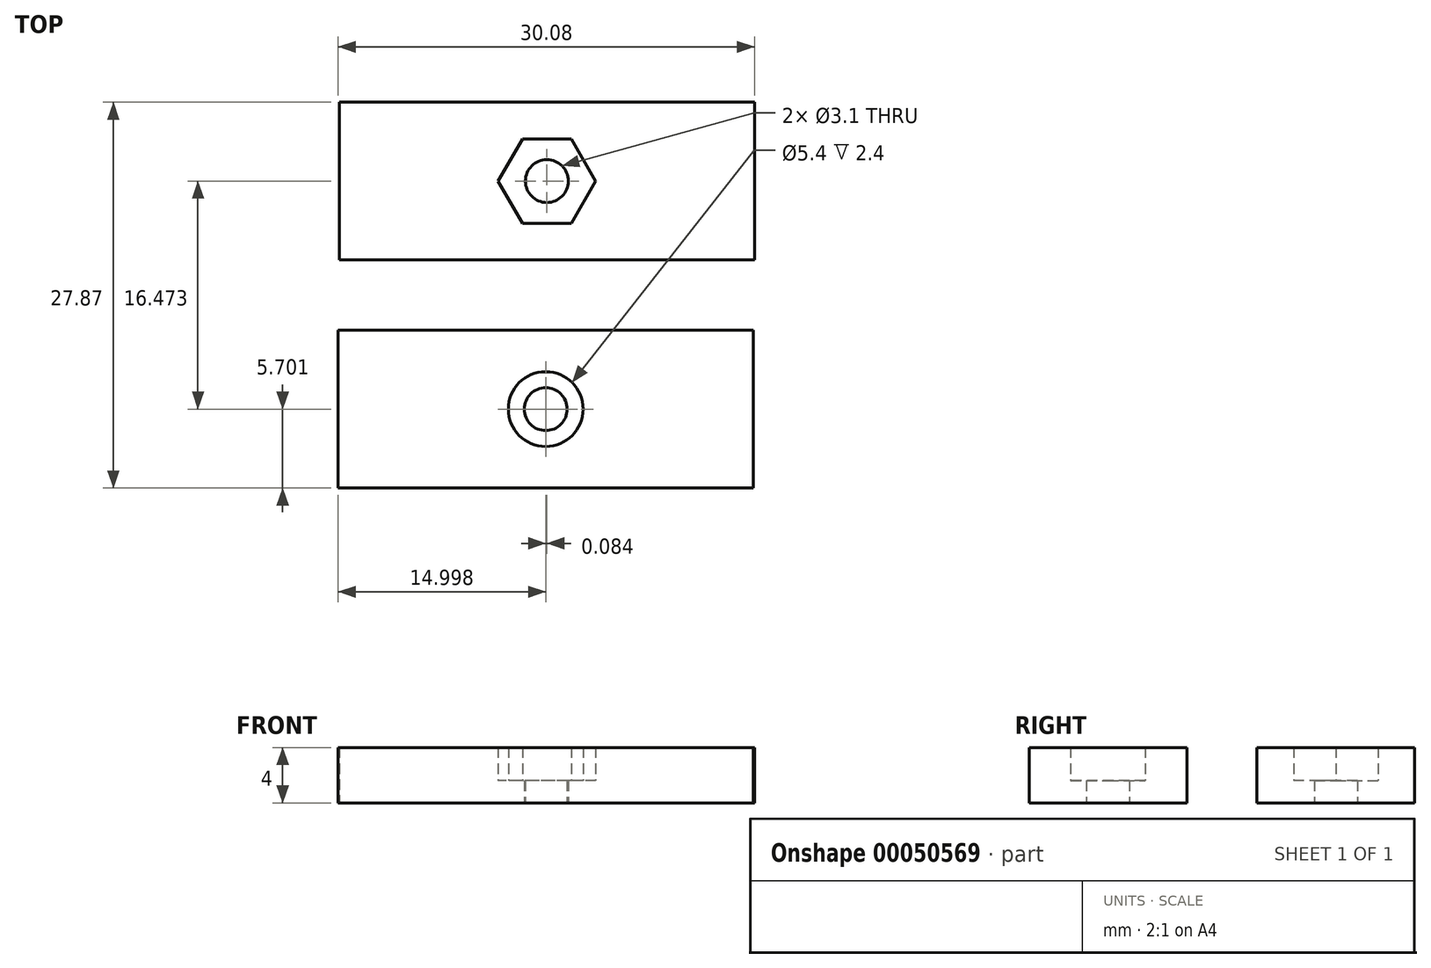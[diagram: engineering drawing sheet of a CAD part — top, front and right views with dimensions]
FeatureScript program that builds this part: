
annotation { "Feature Type Name" : "Feature", "Feature Type Description" : "" }
export const myFeature = defineFeature(function(context is Context, id is Id, definition is map)
    precondition{}
    {
        {
            var Q0;
            Q0=qCreatedBy(makeId("Top.planeOp"),FACE);
            var sketch = newSketch(context, id + "F0", { "sketchPlane" : qUnion([Q0])});
            skLineSegment(sketch, "E0.bottom", {"start": v(-16.18, 3.75) * mm, "end": v(13.82, 3.75) * mm});
            skLineSegment(sketch, "E0.top", {"start": v(-16.18, -7.65) * mm, "end": v(13.82, -7.65) * mm});
            skLineSegment(sketch, "E0.left", {"start": v(-16.18, 3.75) * mm, "end": v(-16.18, -7.65) * mm});
            skLineSegment(sketch, "E0.right", {"start": v(13.82, 3.75) * mm, "end": v(13.82, -7.65) * mm});
            skLineSegment(sketch, "E1", {"start": v(-16.18, -1.95) * mm, "end": v(13.82, -1.95) * mm, "construction": true});
            skPoint(sketch, "E2.start.orphan", {"position": v(-1.18, 3.75) * mm});
            skPoint(sketch, "E3.trimOffspring.end.orphan", {"position": v(-1.18, -7.65) * mm});
            skLineSegment(sketch, "E4.bottom", {"start": v(-16.26, -12.72) * mm, "end": v(13.74, -12.72) * mm});
            skLineSegment(sketch, "E4.top", {"start": v(-16.26, -24.12) * mm, "end": v(13.74, -24.12) * mm});
            skLineSegment(sketch, "E4.left", {"start": v(-16.26, -12.72) * mm, "end": v(-16.26, -24.12) * mm});
            skLineSegment(sketch, "E4.right", {"start": v(13.74, -12.72) * mm, "end": v(13.74, -24.12) * mm});
            skLineSegment(sketch, "E5", {"start": v(-16.26, -18.42) * mm, "end": v(13.74, -18.42) * mm, "construction": true});
            skLineSegment(sketch, "E6.bottom", {"start": v(-30.6, 1.86) * mm, "end": v(-19.57, 1.86) * mm, "construction": true});
            skLineSegment(sketch, "E6.top", {"start": v(-30.6, -8.16) * mm, "end": v(-19.57, -8.16) * mm, "construction": true});
            skLineSegment(sketch, "E6.left", {"start": v(-30.6, 1.86) * mm, "end": v(-30.6, -8.16) * mm, "construction": true});
            skLineSegment(sketch, "E6.right", {"start": v(-19.57, 1.86) * mm, "end": v(-19.57, -8.16) * mm, "construction": true});
            skLineSegment(sketch, "E7", {"start": v(-30.6, -3.15) * mm, "end": v(-19.57, -3.15) * mm, "construction": true});
            skCircle(sketch, "E8", {"center": v(-25.09, -3.15) * mm, "radius": 1.55 * mm, "construction": true});
            skCircle(sketch, "E9", {"center": v(-25.09, -3.15) * mm, "radius": 2.85 * mm, "construction": true});
            skLineSegment(sketch, "E10.0", {"start": v(-23.44, -6) * mm, "end": v(-26.73, -6) * mm});
            skLineSegment(sketch, "E10.1", {"start": v(-26.73, -6) * mm, "end": v(-28.38, -3.15) * mm});
            skLineSegment(sketch, "E10.2", {"start": v(-28.38, -3.15) * mm, "end": v(-26.73, -0.3) * mm});
            skLineSegment(sketch, "E10.3", {"start": v(-26.73, -0.3) * mm, "end": v(-23.44, -0.3) * mm});
            skLineSegment(sketch, "E10.4", {"start": v(-23.44, -0.3) * mm, "end": v(-21.8, -3.15) * mm});
            skLineSegment(sketch, "E10.5", {"start": v(-21.8, -3.15) * mm, "end": v(-23.44, -6) * mm});
            skPoint(sketch, "E10.0.midPoint", {"position": v(-25.09, -6) * mm});
            skLineSegment(sketch, "E11.bottom", {"start": v(-30.75, -10.5) * mm, "end": v(-19.53, -10.5) * mm, "construction": true});
            skLineSegment(sketch, "E11.top", {"start": v(-30.75, -21.36) * mm, "end": v(-19.53, -21.36) * mm, "construction": true});
            skLineSegment(sketch, "E11.left", {"start": v(-30.75, -10.5) * mm, "end": v(-30.75, -21.36) * mm, "construction": true});
            skLineSegment(sketch, "E11.right", {"start": v(-19.53, -10.5) * mm, "end": v(-19.53, -21.36) * mm, "construction": true});
            skLineSegment(sketch, "E12", {"start": v(-30.75, -15.93) * mm, "end": v(-19.53, -15.93) * mm, "construction": true});
            skCircle(sketch, "E13", {"center": v(-25.14, -15.93) * mm, "radius": 1.55 * mm, "construction": true});
            skCircle(sketch, "E14", {"center": v(-25.14, -15.93) * mm, "radius": 2.8 * mm, "construction": true});
            skLineSegment(sketch, "E15", {"start": v(-1.26, -24.12) * mm, "end": v(-1.26, -21.12) * mm, "construction": true});
            skLineSegment(sketch, "E16", {"start": v(-1.26, -12.72) * mm, "end": v(-1.26, -15.72) * mm, "construction": true});
            skLineSegment(sketch, "E17", {"start": v(-1.18, 3.75) * mm, "end": v(-1.18, 0.75) * mm, "construction": true});
            skLineSegment(sketch, "E18", {"start": v(-1.18, -7.65) * mm, "end": v(-1.18, -5) * mm, "construction": true});
            skCircle(sketch, "E19", {"center": v(-1.18, -1.95) * mm, "radius": 1.55 * mm});
            skCircle(sketch, "E20", {"center": v(-1.18, -1.95) * mm, "radius": 2.85 * mm, "construction": true});
            skCircle(sketch, "E21.cCircle", {"center": v(-1.18, -1.95) * mm, "radius": 3.05 * mm, "construction": true});
            skLineSegment(sketch, "E21.0", {"start": v(0.58, -5) * mm, "end": v(-2.94, -5) * mm});
            skLineSegment(sketch, "E21.1", {"start": v(-2.94, -5) * mm, "end": v(-4.7, -1.95) * mm});
            skLineSegment(sketch, "E21.2", {"start": v(-4.7, -1.95) * mm, "end": v(-2.94, 1.1) * mm});
            skLineSegment(sketch, "E21.3", {"start": v(-2.94, 1.1) * mm, "end": v(0.58, 1.1) * mm});
            skLineSegment(sketch, "E21.4", {"start": v(0.58, 1.1) * mm, "end": v(2.34, -1.95) * mm});
            skLineSegment(sketch, "E21.5", {"start": v(2.34, -1.95) * mm, "end": v(0.58, -5) * mm});
            skPoint(sketch, "E21.0.midPoint", {"position": v(-1.18, -5) * mm});
            skCircle(sketch, "E22", {"center": v(-1.26, -18.42) * mm, "radius": 1.55 * mm});
            skCircle(sketch, "E23", {"center": v(-1.26, -18.42) * mm, "radius": 2.7 * mm});
            skSolve(sketch);
        }
        {
            var Q0;
            Q0=makeQuery(id+"F0.imprint","IMPRINT",FACE,{"disambiguationData":[TD([[makeQuery(id+"F0.imprint","IMPRINT",EDGE,{"derivedFrom":sQuery(id+"F0.wireOp",EDGE,"E0.bottom")}),-1.0]])]});
            var Q1;
            Q1=makeQuery(id+"F0.imprint","IMPRINT",FACE,{"disambiguationData":[TD([[makeQuery(id+"F0.imprint","IMPRINT",EDGE,{"derivedFrom":sQuery(id+"F0.wireOp",EDGE,"E4.bottom")}),-1.0]])]});
            extrude(context, id + "F1", {"entities" : qUnion([Q0, Q1]), "depth" : 4 * mm});
        }
        {
            var Q0;
            Q0=makeQuery(id+"F0.imprint","IMPRINT",FACE,{"disambiguationData":[TD([[makeQuery(id+"F0.imprint","IMPRINT",EDGE,{"derivedFrom":sQuery(id+"F0.wireOp",EDGE,"E19")}),-1.0]])]});
            var Q1;
            Q1=makeQuery(id+"F0.imprint","IMPRINT",FACE,{"disambiguationData":[TD([[makeQuery(id+"F0.imprint","IMPRINT",EDGE,{"derivedFrom":sQuery(id+"F0.wireOp",EDGE,"E22")}),-1.0]])]});
            extrude(context, id + "F2", {"entities" : qUnion([Q0, Q1]), "operationType" : NewBodyOperationType.ADD, "depth" : 1.6 * mm});
        }
    });
